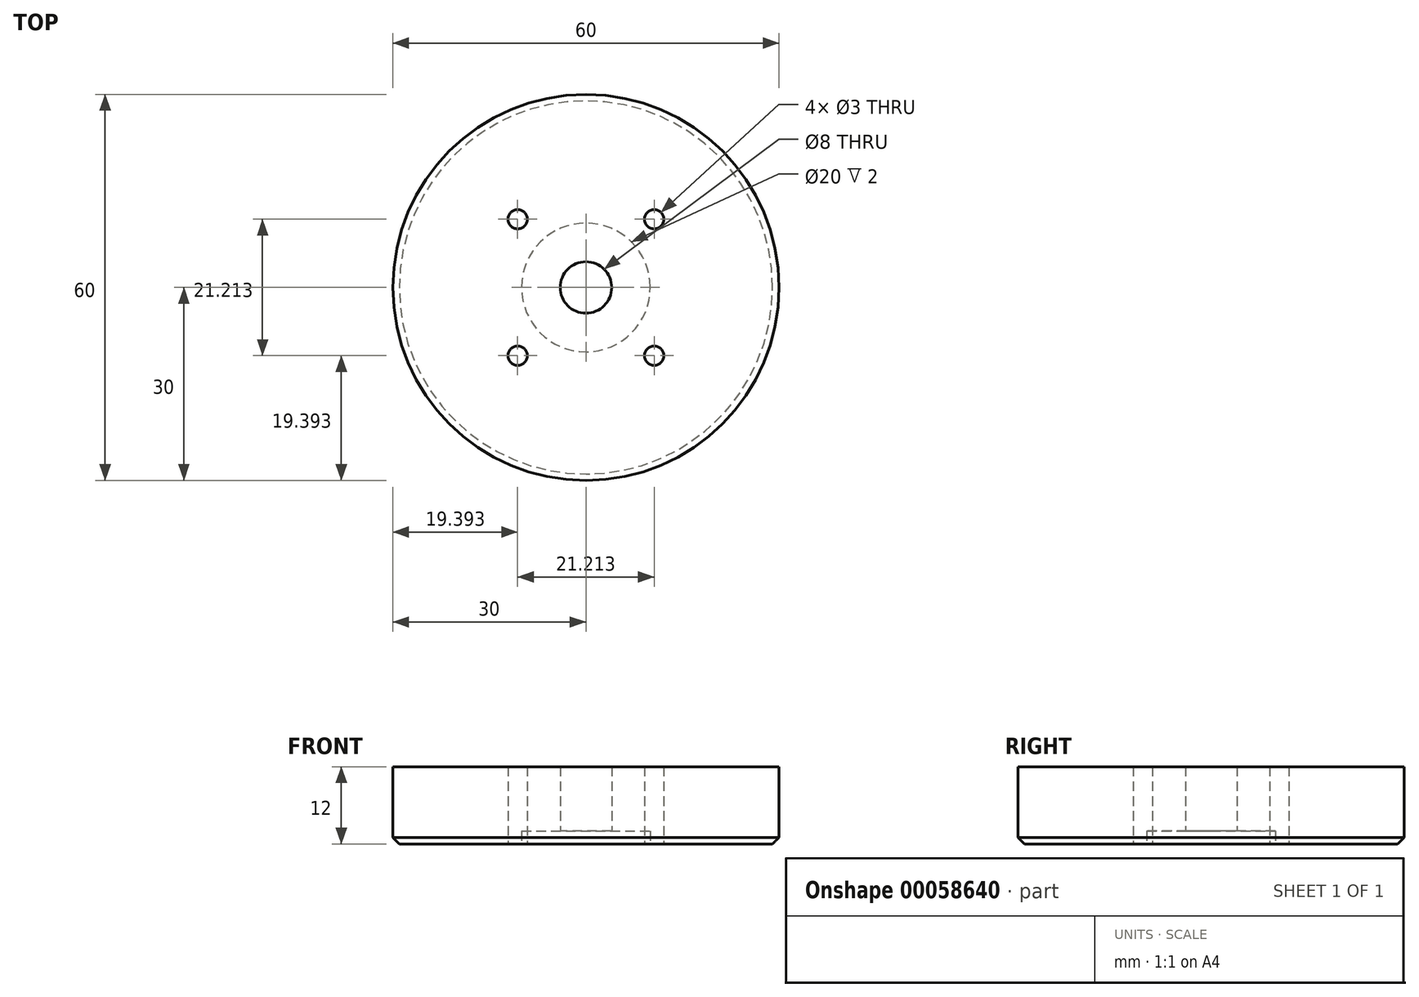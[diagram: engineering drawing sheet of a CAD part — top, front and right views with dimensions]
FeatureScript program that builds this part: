
annotation { "Feature Type Name" : "Feature", "Feature Type Description" : "" }
export const myFeature = defineFeature(function(context is Context, id is Id, definition is map)
    precondition{}
    {
        {
            var Q0;
            Q0=qCreatedBy(makeId("Top.planeOp"),FACE);
            var sketch = newSketch(context, id + "F0", { "sketchPlane" : qUnion([Q0])});
            skCircle(sketch, "E0", {"center": v(0, 0) * mm, "radius": 30 * mm});
            skCircle(sketch, "E1", {"center": v(0, 0) * mm, "radius": 4 * mm});
            skCircle(sketch, "E2", {"center": v(-10.6, 10.6) * mm, "radius": 1.5 * mm});
            skCircle(sketch, "E3", {"center": v(10.6, 10.6) * mm, "radius": 1.5 * mm});
            skCircle(sketch, "E4", {"center": v(10.6, -10.6) * mm, "radius": 1.5 * mm});
            skCircle(sketch, "E5", {"center": v(-10.6, -10.6) * mm, "radius": 1.5 * mm});
            skSolve(sketch);
        }
        {
            var Q0;
            Q0=qSketchRegion(id+"F0",true);
            extrude(context, id + "F1", {"entities" : qUnion([Q0]), "depth" : 12 * mm});
        }
        {
            var Q0;
            Q0=makeQuery(id+"F1.opExtrude","CAP_EDGE",EDGE,{"disambiguationData":[OSD([sQuery(id+"F0.wireOp",EDGE,"E0")])],"isStart":true});
            chamfer(context, id + "F2", {"entities" : qUnion([Q0]), "width" : 1 * mm, "tangentPropagation" : true});
        }
        {
            var Q0;
            Q0=makeQuery(id+"F1.opExtrude","CAP_FACE",FACE,{"disambiguationData":[OSD([sQuery(id+"F0.wireOp",EDGE,"E0"),sQuery(id+"F0.wireOp",EDGE,"E1"),sQuery(id+"F0.wireOp",EDGE,"E2"),sQuery(id+"F0.wireOp",EDGE,"E3"),sQuery(id+"F0.wireOp",EDGE,"E4"),sQuery(id+"F0.wireOp",EDGE,"E5")])],"isStart":true});
            var sketch = newSketch(context, id + "F3", { "sketchPlane" : qUnion([Q0])});
            skCircle(sketch, "E6", {"center": v(0, 0) * mm, "radius": 10 * mm});
            skSolve(sketch);
        }
        {
            var Q0;
            Q0=makeQuery(id+"F3.imprint","IMPRINT",FACE,{"disambiguationData":[TD([[makeQuery(id+"F3.imprint","IMPRINT",EDGE,{"derivedFrom":sQuery(id+"F3.wireOp",EDGE,"E6")}),1.0]])]});
            extrude(context, id + "F4", {"entities" : qUnion([Q0]), "operationType" : NewBodyOperationType.REMOVE, "oppositeDirection" : true, "depth" : 2 * mm});
        }
    });
